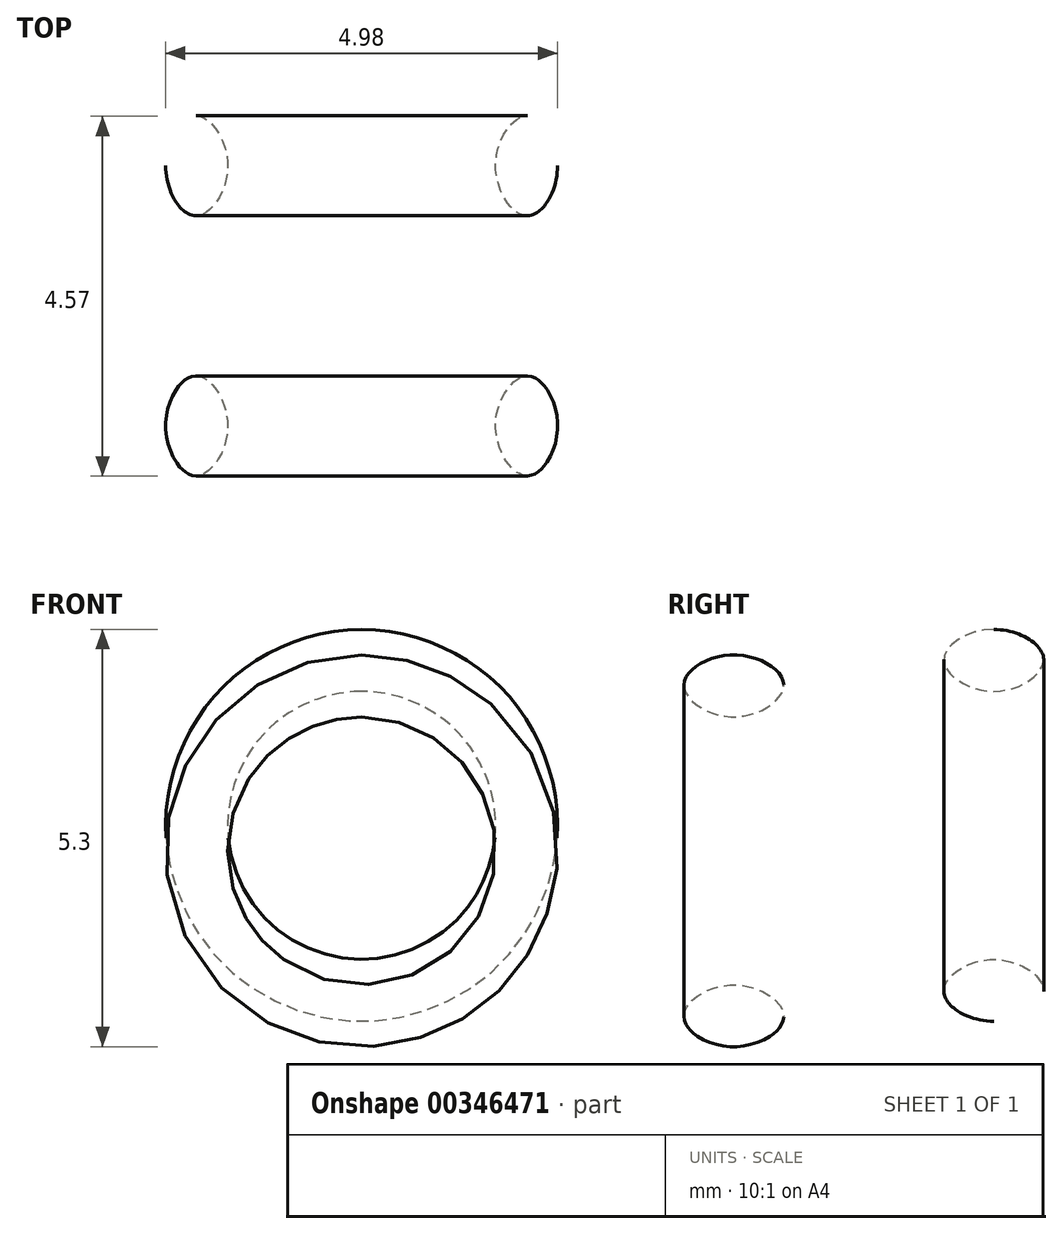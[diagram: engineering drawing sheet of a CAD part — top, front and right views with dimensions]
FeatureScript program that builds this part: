
annotation { "Feature Type Name" : "Feature", "Feature Type Description" : "" }
export const myFeature = defineFeature(function(context is Context, id is Id, definition is map)
    precondition{}
    {
        {
            var Q0;
            Q0=qCreatedBy(makeId("Right.planeOp"),FACE);
            var sketch = newSketch(context, id + "F0", { "sketchPlane" : qUnion([Q0])});
            skLineSegment(sketch, "E0", {"start": v(-4.97, 8.64) * mm, "end": v(-4.97, 7.85) * mm, "construction": true});
            skLineSegment(sketch, "E1", {"start": v(-5.6, 8.26) * mm, "end": v(-4.34, 8.26) * mm, "construction": true});
            skFitSpline(sketch, "E2", {"points": [v(-4.97, 8.64) * mm, v(-5.6, 8.26) * mm, v(-4.97, 7.85) * mm, v(-4.34, 8.26) * mm, v(-4.97, 8.64) * mm]});
            skLineSegment(sketch, "E3", {"start": v(-6.9, 6.15) * mm, "end": v(-2.88, 6.15) * mm, "construction": true});
            skSolve(sketch);
        }
        {
            var Q0;
            Q0=makeQuery(id+"F0.imprint","IMPRINT",FACE,{"disambiguationData":[TD([[makeQuery(id+"F0.imprint","IMPRINT",EDGE,{"derivedFrom":sQuery(id+"F0.wireOp",EDGE,"E2")}),1.0]])]});
            var Q1;
            Q1=sQuery(id+"F0.wireOp",EDGE,"E3");
            revolve(context, id + "F1", {"surfaceOperationType" : NewSurfaceOperationType.NEW, "entities" : qUnion([Q0]), "axis" : qUnion([Q1]), "revolveType" : RevolveType.FULL});
        }
        {
            var Q0;
            Q0=qCreatedBy(makeId("Right.planeOp"),FACE);
            var sketch = newSketch(context, id + "F2", { "sketchPlane" : qUnion([Q0])});
            skLineSegment(sketch, "E4", {"start": v(-8.27, 8.32) * mm, "end": v(-8.27, 7.53) * mm, "construction": true});
            skLineSegment(sketch, "E5", {"start": v(-8.9, 7.94) * mm, "end": v(-7.64, 7.94) * mm, "construction": true});
            skFitSpline(sketch, "E6", {"points": [v(-7.64, 7.94) * mm, v(-8.27, 8.32) * mm, v(-8.9, 7.94) * mm, v(-8.27, 7.53) * mm, v(-7.64, 7.94) * mm]});
            skLineSegment(sketch, "E7", {"start": v(-9.54, 5.83) * mm, "end": v(-6.78, 5.83) * mm, "construction": true});
            skSolve(sketch);
        }
        {
            var Q0;
            Q0=makeQuery(id+"F2.imprint","IMPRINT",FACE,{"disambiguationData":[TD([[makeQuery(id+"F2.imprint","IMPRINT",EDGE,{"derivedFrom":sQuery(id+"F2.wireOp",EDGE,"E6")}),1.0]])]});
            var Q1;
            Q1=sQuery(id+"F2.wireOp",EDGE,"E7");
            revolve(context, id + "F3", {"surfaceOperationType" : NewSurfaceOperationType.NEW, "entities" : qUnion([Q0]), "axis" : qUnion([Q1]), "revolveType" : RevolveType.FULL});
        }
    });
